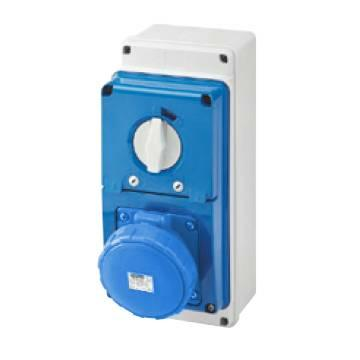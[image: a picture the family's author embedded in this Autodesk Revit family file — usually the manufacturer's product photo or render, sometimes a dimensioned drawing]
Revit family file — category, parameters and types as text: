
# Revit family: Building-IEC309Connections-GEWISS-67IB-INTERLOCKED-SOCKET-OUTLETS_IP67_WITH_BOTTOM_63A_FUS
name_source: partatom
category: Apparecchi elettrici
revit_build: Autodesk Revit 2016 (Build: 20161004_0715(x64)
units: mm (PartAtom-declared; Revit-internal decimal feet)

## family parameters
Condiviso = No
Host = Muro
Mantenere orientamento annotazione = Sì
Numero OmniClass = 23.80.50.14
Punto di calcolo locali = No
Quota connettore circolare = Usa diametro
Sempre verticale = Sì
Taglio con vuoti quando caricato = No
Tipo di parte = Normale
Titolo OmniClass = Plug Connectors

## types (11) — shared parameters
Altezza da terra = 1112 mm
Carico apparente = 0 VA
Catalogue = BUILDING
Catalogue Range = 67 IB
Classificazione carico = Altro
Electrocod = 2222
Frequency = 50/60 Hz
Fuse breacking capacity = > 50 kA
Glow Wire Test = 850 °C (IB socket) - 650 °C (bottom)
Glow wire test: = 850 °C (IB socket) - 650 °C (bottom)
IDF = 1711c5f6-abc8-487c-ac1f-1400d1f361c6
IDT = c3a9b50e-4e9d-4f00-afb7-28748640f89d
IP degree = IP67
Immagine tipo = GW67254N.jpg
Numero poli = 3
Operating temperature: = -25 +40 °C
Potenza = 500 V
Presa = GEWISS - NERO
Produttore = GEWISS S.p.A.
Protection = Fuse-holder base (CBF)
Rated current (A) = 63
Rated current (In) = 63
Rated frequency (Hz) = 50/60 Hz
Rated impulse withstand voltage = 4KV
Rated insulation voltage (Ui) = 500V
Rated short-circuit current (Icc) = 10KA
SEO = Socket outlet
Shock resistance = IK08
Struttura = GEWISS - Grigio RAL - 7035
Struttura frontale = GEWISS -BLU
Technical sheet = https://www.gewiss.com
Thermo-pressure with ball = 125 °C (IB socket) - 80 °C (bottom)
Tipo Simbolo = PRESAINDPFUS : 3P
Type of fuse = Ã˜ 22x58 mm
Typology = Vertical
URL = https://www.gewiss.com
Version file RFA = 18.0
Vetro = GEWISS - vetro
Weight = Max. 2.5 Kg
Weight (kg) = Max. 2.5 Kg
With back-mounting box = Yes
Working temperature = -25 ÷ +40 °C

## per-type parameters (varying)
| type | Colour | Colour: | Descrizione | EAN code | IB socket outlet rated current (In) | Modello | No. of poles | Number of poles | Rated voltage | Rated voltage: | Reference h |
| GW67246N - 3P+E 63A 110V V.INT.SOCK.O.W.B.4H CBF | Yellow | Yellow | 3P+E 63A 110V V.INT.SOCK.O.W.B.4H CBF | 8011564742161 | 52A | GW67246N | 3P+E | 3P+E | 100 - 130 V | 100 - 130 V | 4 |
| GW67245N - 2P+E 63A 110V V.INT.SOCK.O.W.B.4H CBF | Yellow | Yellow | 2P+E 63A 110V V.INT.SOCK.O.W.B.4H CBF | 8011564742154 | 54A | GW67245N | 2P+E | 2P+E | 100 - 130 V | 100 - 130 V | 4 |
| GW67250N - 3P+N+T 63A 230V V.INT.SOCK.O.W.B.9H CBF | Blue | Blue | 3P+N+T 63A 230V V.INT.SOCK.O.W.B.9H CBF | 8011564742208 | 48A | GW67250N | 3P+N+E | 3P+N+E | 200 - 250 V | 200 - 250 V | 9 |
| GW67255N - 3P+N+T 63A 500V V.INT.SOCK.O.W.B.7H CBF | Black | Black | 3P+N+T 63A 500V V.INT.SOCK.O.W.B.7H CBF | 8011564742253 | 48A | GW67255N | 3P+N+E | 3P+N+E | 480 - 500 V | 480 - 500 V | 7 |
| GW67249N - 3P+E 63A 230V V.INT.SOCK.O.W.B.9H CBF | Blue | Blue | 3P+E 63A 230V V.INT.SOCK.O.W.B.9H CBF | 8011564742192 | 52A | GW67249N | 3P+E | 3P+E | 200 - 250 V | 200 - 250 V | 9 |
| GW67247N - 3P+N+T 63A 110V V.INT.SOCK.O.W.B.4H CBF | Yellow | Yellow | 3P+N+T 63A 110V V.INT.SOCK.O.W.B.4H CBF | 8011564742178 | 48A | GW67247N | 3P+N+E | 3P+N+E | 100 - 130 V | 100 - 130 V | 4 |
| GW67254N - 3P+E 63A 500V V.INT.SOCK.O.W.B.7H CBF | Black | Black | 3P+E 63A 500V V.INT.SOCK.O.W.B.7H CBF | 8011564742246 | 52A | GW67254N | 3P+E | 3P+E | 480 - 500 V | 480 - 500 V | 7 |
| GW67252N - 3P+E 63A 400V V.INT.SOCK.O.W.B.6H CBF | Red | Red | 3P+E 63A 400V V.INT.SOCK.O.W.B.6H CBF | 8011564742222 | 52A | GW67252N | 3P+E | 3P+E | 380 - 415 V | 380 - 415 V | 6 |
| GW67248N - 2P+E 63A 230V V.INT.SOCK.O.W.B.6H CBF | Blue | Blue | 2P+E 63A 230V V.INT.SOCK.O.W.B.6H CBF | 8011564742185 | 54A | GW67248N | 2P+E | 2P+E | 200 - 250 V | 200 - 250 V | 6 |
| GW67253N - 3P+N+T 63A 400V V.INT.SOCK.O.W.B.6H CBF | Red | Red | 3P+N+T 63A 400V V.INT.SOCK.O.W.B.6H CBF | 8011564742239 | 48A | GW67253N | 3P+N+E | 3P+N+E | 380 - 415 V | 380 - 415 V | 6 |
| GW67251N - 2P+E 63A 400V V.INT.SOCK.O.W.B.9H CBF | Red | Red | 2P+E 63A 400V V.INT.SOCK.O.W.B.9H CBF | 8011564742215 | 54A | GW67251N | 2P+E | 2P+E | 380 - 415 V | 380 - 415 V | 9 |

## geometry (parser evidence)
native form markers: Blend x2, Sweep x2
no freeform markers — native parametric forms only
